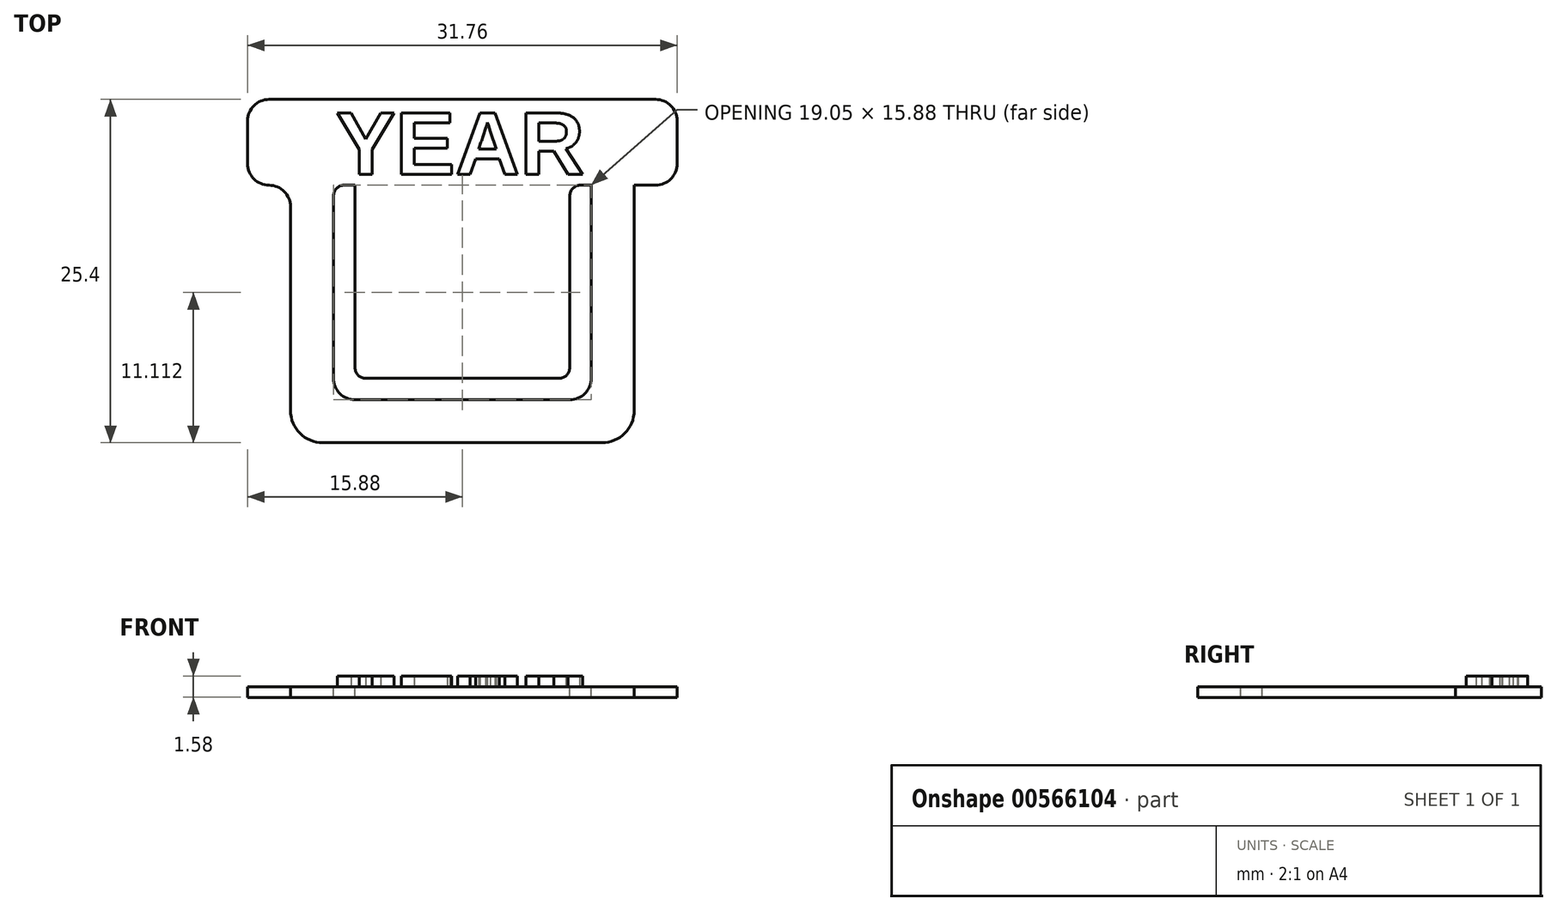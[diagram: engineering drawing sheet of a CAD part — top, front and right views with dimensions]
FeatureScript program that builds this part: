
annotation { "Feature Type Name" : "Feature", "Feature Type Description" : "" }
export const myFeature = defineFeature(function(context is Context, id is Id, definition is map)
    precondition{}
    {
        {
            var Q0;
            Q0=qCreatedBy(makeId("Front.planeOp"),FACE);
            var sketch = newSketch(context, id + "F0", { "sketchPlane" : qUnion([Q0])});
            skLineSegment(sketch, "E0.bottom", {"start": v(12.7, 9.53) * mm, "end": v(-12.7, 9.53) * mm});
            skLineSegment(sketch, "E0.top", {"start": v(12.7, -9.53) * mm, "end": v(-12.7, -9.53) * mm});
            skLineSegment(sketch, "E0.left", {"start": v(12.7, 9.53) * mm, "end": v(12.7, -9.53) * mm});
            skLineSegment(sketch, "E0.right", {"start": v(-12.7, 9.53) * mm, "end": v(-12.7, -9.53) * mm});
            skPoint(sketch, "E0.middle", {"position": v(0, 0) * mm});
            skSolve(sketch);
        }
        {
            var Q0;
            Q0=makeQuery(id+"F0.imprint","IMPRINT",FACE,{"disambiguationData":[TD([[makeQuery(id+"F0.imprint","IMPRINT",EDGE,{"derivedFrom":sQuery(id+"F0.wireOp",EDGE,"E0.bottom")}),1.0]])]});
            extrude(context, id + "F1", {"entities" : qUnion([Q0]), "depth" : 0.8 * mm, "offsetDistance" : 25.4 * mm});
        }
        {
            var Q0;
            Q0=makeQuery(id+"F1.opExtrude","SWEPT_EDGE",EDGE,{"disambiguationData":[OSD([sQuery(id+"F0.wireOp",EDGE,"E0.top"),sQuery(id+"F0.wireOp",EDGE,"E0.left")])]});
            var Q1;
            Q1=makeQuery(id+"F1.opExtrude","SWEPT_EDGE",EDGE,{"disambiguationData":[OSD([sQuery(id+"F0.wireOp",EDGE,"E0.top"),sQuery(id+"F0.wireOp",EDGE,"E0.right")])]});
            fillet(context, id + "F2", {"entities" : qUnion([Q0, Q1]), "radius" : 2.38 * mm, "tangentPropagation" : true, "allowEdgeOverflow" : false});
        }
        {
            var Q0;
            Q0=makeQuery(id+"F1.opExtrude","CAP_FACE",FACE,{"disambiguationData":[OSD([sQuery(id+"F0.wireOp",EDGE,"E0.bottom"),sQuery(id+"F0.wireOp",EDGE,"E0.top"),sQuery(id+"F0.wireOp",EDGE,"E0.left"),sQuery(id+"F0.wireOp",EDGE,"E0.right")])],"isStart":false});
            var sketch = newSketch(context, id + "F3", { "sketchPlane" : qUnion([Q0])});
            skLineSegment(sketch, "E1.bottom", {"start": v(9.52, 9.53) * mm, "end": v(-9.53, 9.53) * mm});
            skLineSegment(sketch, "E1.top", {"start": v(9.53, -6.35) * mm, "end": v(-9.53, -6.35) * mm});
            skLineSegment(sketch, "E1.left", {"start": v(9.52, 9.53) * mm, "end": v(9.53, -6.35) * mm});
            skLineSegment(sketch, "E1.right", {"start": v(-9.53, 9.53) * mm, "end": v(-9.52, -6.35) * mm});
            skPoint(sketch, "E1.middle", {"position": v(0, 0) * mm});
            skSolve(sketch);
        }
        {
            var Q0;
            Q0=makeQuery(id+"F3.imprint","IMPRINT",FACE,{"disambiguationData":[TD([[makeQuery(id+"F3.imprint","IMPRINT",EDGE,{"derivedFrom":sQuery(id+"F3.wireOp",EDGE,"E1.bottom")}),1.0]])]});
            extrude(context, id + "F4", {"entities" : qUnion([Q0]), "operationType" : NewBodyOperationType.REMOVE, "oppositeDirection" : true, "depth" : 4.93 * mm, "offsetDistance" : 25.4 * mm});
        }
        {
            var Q0;
            Q0=makeQuery(id+"F1.opExtrude","CAP_FACE",FACE,{"disambiguationData":[OSD([sQuery(id+"F0.wireOp",EDGE,"E0.bottom"),sQuery(id+"F0.wireOp",EDGE,"E0.top"),sQuery(id+"F0.wireOp",EDGE,"E0.left"),sQuery(id+"F0.wireOp",EDGE,"E0.right")])],"isStart":false});
            var sketch = newSketch(context, id + "F5", { "sketchPlane" : qUnion([Q0])});
            skLineSegment(sketch, "E2.bottom", {"start": v(-15.88, 9.53) * mm, "end": v(15.87, 9.53) * mm});
            skLineSegment(sketch, "E2.top", {"start": v(-15.88, 15.88) * mm, "end": v(15.87, 15.88) * mm});
            skLineSegment(sketch, "E2.left", {"start": v(-15.88, 9.53) * mm, "end": v(-15.88, 15.88) * mm});
            skLineSegment(sketch, "E2.right", {"start": v(15.87, 9.53) * mm, "end": v(15.87, 15.88) * mm});
            skSolve(sketch);
        }
        {
            var Q0;
            Q0=makeQuery(id+"F5.imprint","IMPRINT",FACE,{"disambiguationData":[TD([[makeQuery(id+"F5.imprint","IMPRINT",EDGE,{"derivedFrom":sQuery(id+"F5.wireOp",EDGE,"E2.top")}),-1.0]])]});
            extrude(context, id + "F6", {"entities" : qUnion([Q0]), "operationType" : NewBodyOperationType.ADD, "oppositeDirection" : true, "depth" : 0.8 * mm, "offsetDistance" : 25.4 * mm});
        }
        {
            var Q0;
            Q0=makeQuery(id+"F6.opExtrude","SWEPT_EDGE",EDGE,{"disambiguationData":[OSD([sQuery(id+"F5.wireOp",EDGE,"E2.top"),sQuery(id+"F5.wireOp",EDGE,"E2.left")])]});
            var Q1;
            Q1=makeQuery(id+"F6.opExtrude","SWEPT_EDGE",EDGE,{"disambiguationData":[OSD([sQuery(id+"F5.wireOp",EDGE,"E2.top"),sQuery(id+"F5.wireOp",EDGE,"E2.right")])]});
            var Q2;
            Q2=makeQuery(id+"F6.opExtrude","SWEPT_EDGE",EDGE,{"disambiguationData":[OSD([sQuery(id+"F5.wireOp",EDGE,"E2.bottom"),sQuery(id+"F5.wireOp",EDGE,"E2.right")])]});
            var Q3;
            Q3=makeQuery(id+"F1.opExtrude","SWEPT_EDGE",EDGE,{"disambiguationData":[OSD([sQuery(id+"F0.wireOp",EDGE,"E0.bottom"),sQuery(id+"F0.wireOp",EDGE,"E0.left")])]});
            var Q4;
            Q4=makeQuery(id+"F6.opExtrude","SWEPT_EDGE",EDGE,{"disambiguationData":[OSD([sQuery(id+"F5.wireOp",EDGE,"E2.bottom"),sQuery(id+"F5.wireOp",EDGE,"E2.left")])]});
            var Q5;
            Q5=makeQuery(id+"F1.opExtrude","SWEPT_EDGE",EDGE,{"disambiguationData":[OSD([sQuery(id+"F0.wireOp",EDGE,"E0.bottom"),sQuery(id+"F0.wireOp",EDGE,"E0.right")])]});
            fillet(context, id + "F7", {"entities" : qUnion([Q0, Q1, Q2, Q3, Q4, Q5]), "radius" : 1.59 * mm, "tangentPropagation" : true, "allowEdgeOverflow" : false});
        }
        {
            var Q0;
            Q0=makeQuery(id+"F4.boolean.opBoolean","COPY",EDGE,{"derivedFrom":makeQuery(id+"F4.opExtrude","SWEPT_EDGE",EDGE,{"disambiguationData":[OSD([sQuery(id+"F3.wireOp",EDGE,"E1.top"),sQuery(id+"F3.wireOp",EDGE,"E1.right")])]})});
            var Q1;
            Q1=makeQuery(id+"F4.boolean.opBoolean","COPY",EDGE,{"derivedFrom":makeQuery(id+"F4.opExtrude","SWEPT_EDGE",EDGE,{"disambiguationData":[OSD([sQuery(id+"F3.wireOp",EDGE,"E1.top"),sQuery(id+"F3.wireOp",EDGE,"E1.left")])]})});
            fillet(context, id + "F8", {"entities" : qUnion([Q0, Q1]), "radius" : 1.59 * mm, "tangentPropagation" : true, "allowEdgeOverflow" : false});
        }
        {
            var Q0;
            Q0=makeQuery(id+"F6.boolean.opBoolean","MERGE",FACE,{"derivedFrom":[makeQuery(id+"F1.opExtrude","CAP_FACE",FACE,{"disambiguationData":[OSD([sQuery(id+"F0.wireOp",EDGE,"E0.bottom"),sQuery(id+"F0.wireOp",EDGE,"E0.top"),sQuery(id+"F0.wireOp",EDGE,"E0.left"),sQuery(id+"F0.wireOp",EDGE,"E0.right")])],"isStart":false}),makeQuery(id+"F6.opExtrude","CAP_FACE",FACE,{"disambiguationData":[OSD([sQuery(id+"F5.wireOp",EDGE,"E2.bottom"),sQuery(id+"F5.wireOp",EDGE,"E2.top"),sQuery(id+"F5.wireOp",EDGE,"E2.left"),sQuery(id+"F5.wireOp",EDGE,"E2.right")])],"isStart":true})]});
            var sketch = newSketch(context, id + "F9", { "sketchPlane" : qUnion([Q0])});
            skLineSegment(sketch, "E3.bottom", {"start": v(-7.94, 9.53) * mm, "end": v(7.94, 9.53) * mm});
            skLineSegment(sketch, "E3.top", {"start": v(-7.94, -4.76) * mm, "end": v(7.94, -4.76) * mm});
            skLineSegment(sketch, "E3.left", {"start": v(-7.94, 9.53) * mm, "end": v(-7.94, -4.76) * mm});
            skLineSegment(sketch, "E3.right", {"start": v(7.94, 9.53) * mm, "end": v(7.94, -4.76) * mm});
            skSolve(sketch);
        }
        {
            var Q0;
            Q0=makeQuery(id+"F9.imprint","IMPRINT",FACE,{"disambiguationData":[TD([[makeQuery(id+"F9.imprint","IMPRINT",EDGE,{"derivedFrom":sQuery(id+"F9.wireOp",EDGE,"E3.bottom")}),1.0]])]});
            extrude(context, id + "F10", {"entities" : qUnion([Q0]), "operationType" : NewBodyOperationType.ADD, "oppositeDirection" : true, "depth" : 0.8 * mm, "offsetDistance" : 25.4 * mm});
        }
        {
            var Q0;
            Q0=makeQuery(id+"F10.boolean.opBoolean","MERGE",FACE,{"derivedFrom":[makeQuery(id+"F6.boolean.opBoolean","MERGE",FACE,{"derivedFrom":[makeQuery(id+"F1.opExtrude","CAP_FACE",FACE,{"disambiguationData":[OSD([sQuery(id+"F0.wireOp",EDGE,"E0.bottom"),sQuery(id+"F0.wireOp",EDGE,"E0.top"),sQuery(id+"F0.wireOp",EDGE,"E0.left"),sQuery(id+"F0.wireOp",EDGE,"E0.right")])],"isStart":false}),makeQuery(id+"F6.opExtrude","CAP_FACE",FACE,{"disambiguationData":[OSD([sQuery(id+"F5.wireOp",EDGE,"E2.bottom"),sQuery(id+"F5.wireOp",EDGE,"E2.top"),sQuery(id+"F5.wireOp",EDGE,"E2.left"),sQuery(id+"F5.wireOp",EDGE,"E2.right")])],"isStart":true})]}),makeQuery(id+"F10.opExtrude","CAP_FACE",FACE,{"disambiguationData":[OSD([sQuery(id+"F9.wireOp",EDGE,"E3.bottom"),sQuery(id+"F9.wireOp",EDGE,"E3.top"),sQuery(id+"F9.wireOp",EDGE,"E3.left"),sQuery(id+"F9.wireOp",EDGE,"E3.right")])],"isStart":true})]});
            var sketch = newSketch(context, id + "F11", { "sketchPlane" : qUnion([Q0])});
            skText(sketch, "E4", { "text": "YEAR", "fontName": "Arimo-Bold.ttf"});
            const initialGuessF11  = {"E4": [-0.00935, 0.01032, 1, 0, 0.00476]};
            skSetInitialGuess(sketch, initialGuessF11);
            skSolve(sketch);
        }
        {
            var Q0;
            Q0 = qSketchRegion(id + "F11", true);
            extrude(context, id + "F12", {"entities" : qUnion([Q0]), "operationType" : NewBodyOperationType.ADD, "depth" : 0.8 * mm, "offsetDistance" : 25.4 * mm});
        }
        {
            var Q0;
            Q0=makeQuery(id+"F10.opExtrude","SWEPT_EDGE",EDGE,{"disambiguationData":[OSD([sQuery(id+"F5.wireOp",EDGE,"E2.bottom"),sQuery(id+"F9.wireOp",EDGE,"E3.bottom"),sQuery(id+"F9.wireOp",EDGE,"E3.left")])]});
            var Q1;
            Q1=makeQuery(id+"F4.boolean.opBoolean","COPY",EDGE,{"derivedFrom":makeQuery(id+"F4.opExtrude","SWEPT_EDGE",EDGE,{"disambiguationData":[OSD([sQuery(id+"F0.wireOp",EDGE,"E0.bottom"),sQuery(id+"F3.wireOp",EDGE,"E1.bottom"),sQuery(id+"F3.wireOp",EDGE,"E1.right")])]})});
            var Q2;
            Q2=makeQuery(id+"F10.opExtrude","SWEPT_EDGE",EDGE,{"disambiguationData":[OSD([sQuery(id+"F5.wireOp",EDGE,"E2.bottom"),sQuery(id+"F9.wireOp",EDGE,"E3.bottom"),sQuery(id+"F9.wireOp",EDGE,"E3.right")])]});
            var Q3;
            Q3=makeQuery(id+"F4.boolean.opBoolean","COPY",EDGE,{"derivedFrom":makeQuery(id+"F4.opExtrude","SWEPT_EDGE",EDGE,{"disambiguationData":[OSD([sQuery(id+"F0.wireOp",EDGE,"E0.bottom"),sQuery(id+"F3.wireOp",EDGE,"E1.bottom"),sQuery(id+"F3.wireOp",EDGE,"E1.left")])]})});
            fillet(context, id + "F13", {"entities" : qUnion([Q0, Q1, Q2, Q3]), "radius" : 0.8 * mm, "tangentPropagation" : true, "allowEdgeOverflow" : false});
        }
        {
            var Q0;
            Q0=makeQuery(id+"F10.opExtrude","SWEPT_EDGE",EDGE,{"disambiguationData":[OSD([sQuery(id+"F9.wireOp",EDGE,"E3.top"),sQuery(id+"F9.wireOp",EDGE,"E3.left")])]});
            var Q1;
            Q1=makeQuery(id+"F10.opExtrude","SWEPT_EDGE",EDGE,{"disambiguationData":[OSD([sQuery(id+"F9.wireOp",EDGE,"E3.top"),sQuery(id+"F9.wireOp",EDGE,"E3.right")])]});
            fillet(context, id + "F14", {"entities" : qUnion([Q0, Q1]), "radius" : 0.8 * mm, "tangentPropagation" : true, "allowEdgeOverflow" : false});
        }
        {
            var Q0;
            Q0=makeQuery(id+"F1.opExtrude","SWEPT_BODY",BODY,{"disambiguationData":[OSD([sQuery(id+"F0.wireOp",EDGE,"E0.bottom"),sQuery(id+"F0.wireOp",EDGE,"E0.top"),sQuery(id+"F0.wireOp",EDGE,"E0.left"),sQuery(id+"F0.wireOp",EDGE,"E0.right")])]});
            var Q1;
            Q1=makeQuery(id+"F6.opExtrude","CAP_EDGE",EDGE,{"disambiguationData":[OSD([sQuery(id+"F5.wireOp",EDGE,"E2.top")])],"isStart":false});
            transform(context, id + "F15", {"entities" : qUnion([Q0]), "transformType" : TransformType.ROTATION, "transformAxis" : qUnion([Q1]), "angle" : 270 * degree, "makeCopy" : false});
        }
    });
